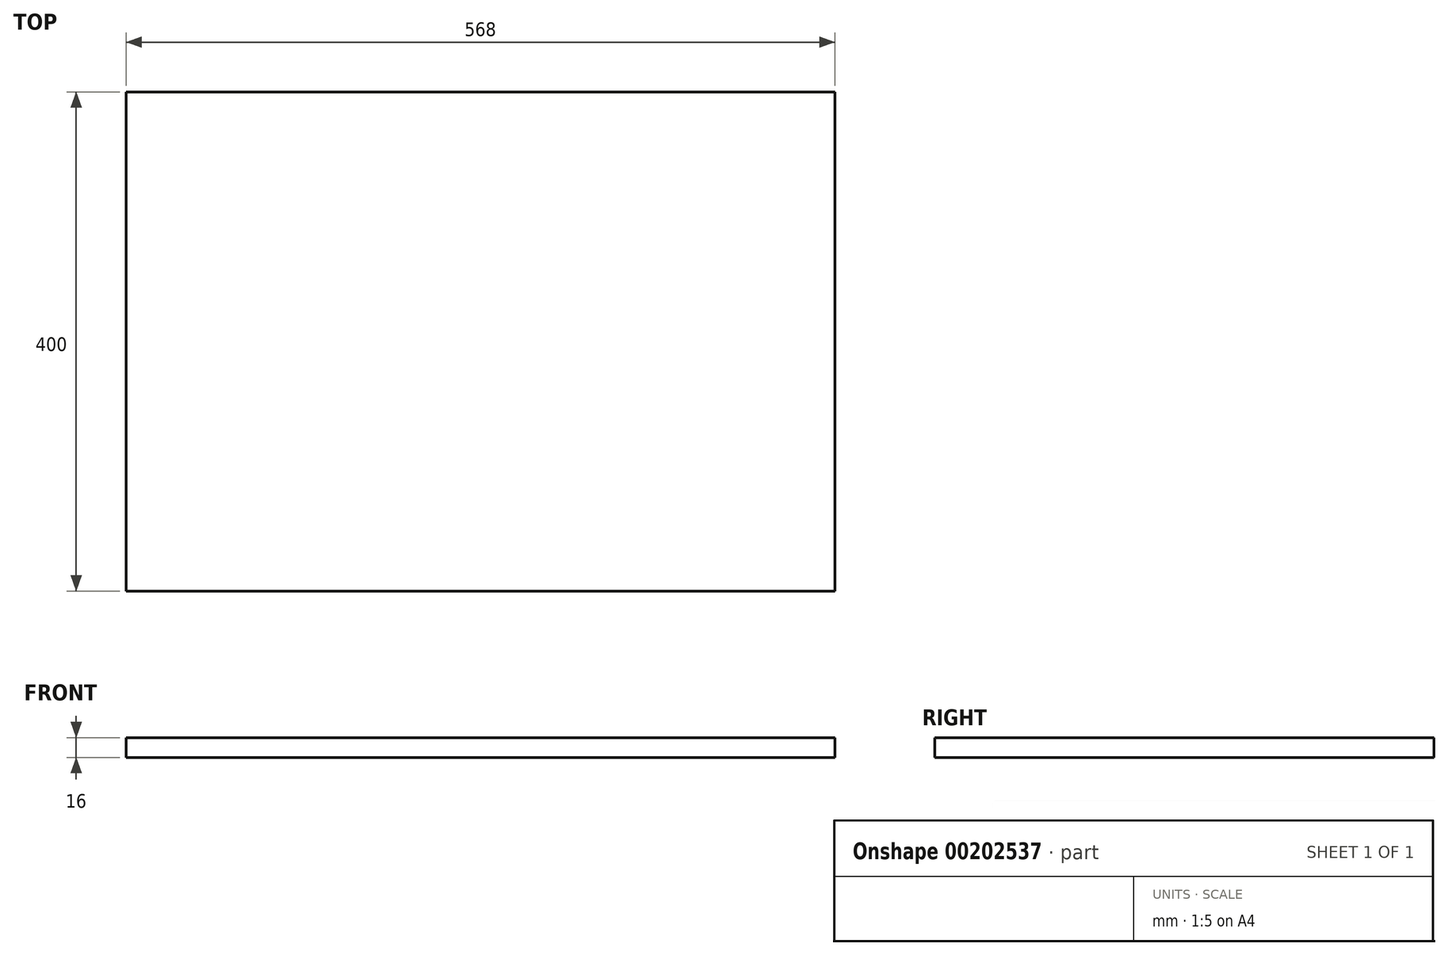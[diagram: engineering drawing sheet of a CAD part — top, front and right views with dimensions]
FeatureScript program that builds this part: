
annotation { "Feature Type Name" : "Feature", "Feature Type Description" : "" }
export const myFeature = defineFeature(function(context is Context, id is Id, definition is map)
    precondition{}
    {
        {
            var Q0;
            Q0=qCreatedBy(makeId("Top.planeOp"),FACE);
            var sketch = newSketch(context, id + "F0", { "sketchPlane" : qUnion([Q0])});
            skLineSegment(sketch, "E0.bottom", {"start": v(-276.3, -87.4) * mm, "end": v(291.7, -87.4) * mm});
            skLineSegment(sketch, "E0.top", {"start": v(-276.3, 312.6) * mm, "end": v(291.7, 312.6) * mm});
            skLineSegment(sketch, "E0.left", {"start": v(-276.3, -87.4) * mm, "end": v(-276.3, 312.6) * mm});
            skLineSegment(sketch, "E0.right", {"start": v(291.7, -87.4) * mm, "end": v(291.7, 312.6) * mm});
            skSolve(sketch);
        }
        {
            var Q0;
            Q0=makeQuery(id+"F0.imprint","IMPRINT",FACE,{"disambiguationData":[TD([[makeQuery(id+"F0.imprint","IMPRINT",EDGE,{"derivedFrom":sQuery(id+"F0.wireOp",EDGE,"E0.bottom")}),1.0]])]});
            extrude(context, id + "F1", {"entities" : qUnion([Q0]), "depth" : 16 * mm});
        }
    });
